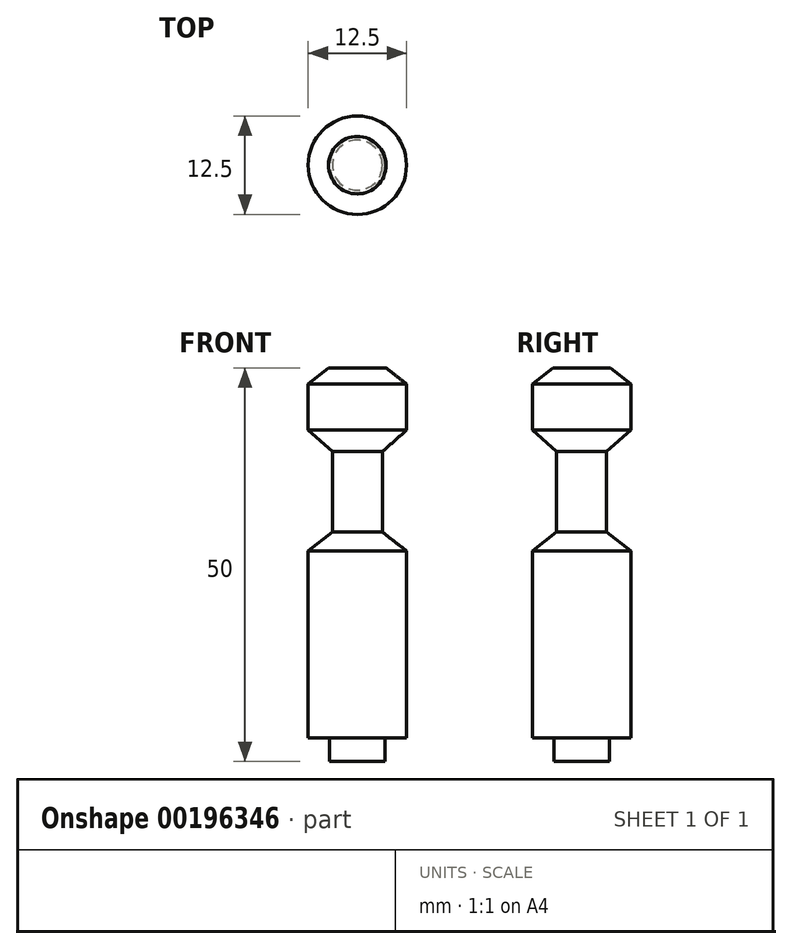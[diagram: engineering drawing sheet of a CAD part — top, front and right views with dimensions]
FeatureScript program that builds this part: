
annotation { "Feature Type Name" : "Feature", "Feature Type Description" : "" }
export const myFeature = defineFeature(function(context is Context, id is Id, definition is map)
    precondition{}
    {
        {
            var Q0;
            Q0=qCreatedBy(makeId("Right.planeOp"),FACE);
            var sketch = newSketch(context, id + "F0", { "sketchPlane" : qUnion([Q0])});
            skLineSegment(sketch, "E0", {"start": v(0, 34.49) * mm, "end": v(0, -15.51) * mm});
            skLineSegment(sketch, "E1", {"start": v(0, -15.51) * mm, "end": v(3.5, -15.51) * mm});
            skLineSegment(sketch, "E2", {"start": v(3.5, -15.51) * mm, "end": v(3.5, -12.51) * mm});
            skLineSegment(sketch, "E3", {"start": v(3.5, -12.51) * mm, "end": v(6.25, -12.51) * mm});
            skLineSegment(sketch, "E4", {"start": v(6.25, -12.51) * mm, "end": v(6.25, 11.24) * mm});
            skLineSegment(sketch, "E5", {"start": v(3.18, 13.64) * mm, "end": v(6.25, 11.24) * mm});
            skLineSegment(sketch, "E6", {"start": v(3.18, 13.64) * mm, "end": v(3.18, 23.86) * mm});
            skLineSegment(sketch, "E7", {"start": v(6.25, 26.57) * mm, "end": v(3.18, 23.86) * mm});
            skLineSegment(sketch, "E8", {"start": v(6.25, 26.57) * mm, "end": v(6.25, 32.45) * mm});
            skLineSegment(sketch, "E9", {"start": v(3.65, 34.49) * mm, "end": v(6.25, 32.45) * mm});
            skLineSegment(sketch, "E10", {"start": v(3.65, 34.49) * mm, "end": v(0, 34.49) * mm});
            skSolve(sketch);
        }
        {
            var Q0;
            Q0=makeQuery(id+"F0.imprint","IMPRINT",FACE,{"disambiguationData":[TD([[makeQuery(id+"F0.imprint","IMPRINT",EDGE,{"derivedFrom":sQuery(id+"F0.wireOp",EDGE,"E0")}),1.0]])]});
            var Q1;
            Q1=sQuery(id+"F0.wireOp",EDGE,"E0");
            revolve(context, id + "F1", {"entities" : qUnion([Q0]), "axis" : qUnion([Q1]), "revolveType" : RevolveType.FULL});
        }
    });
